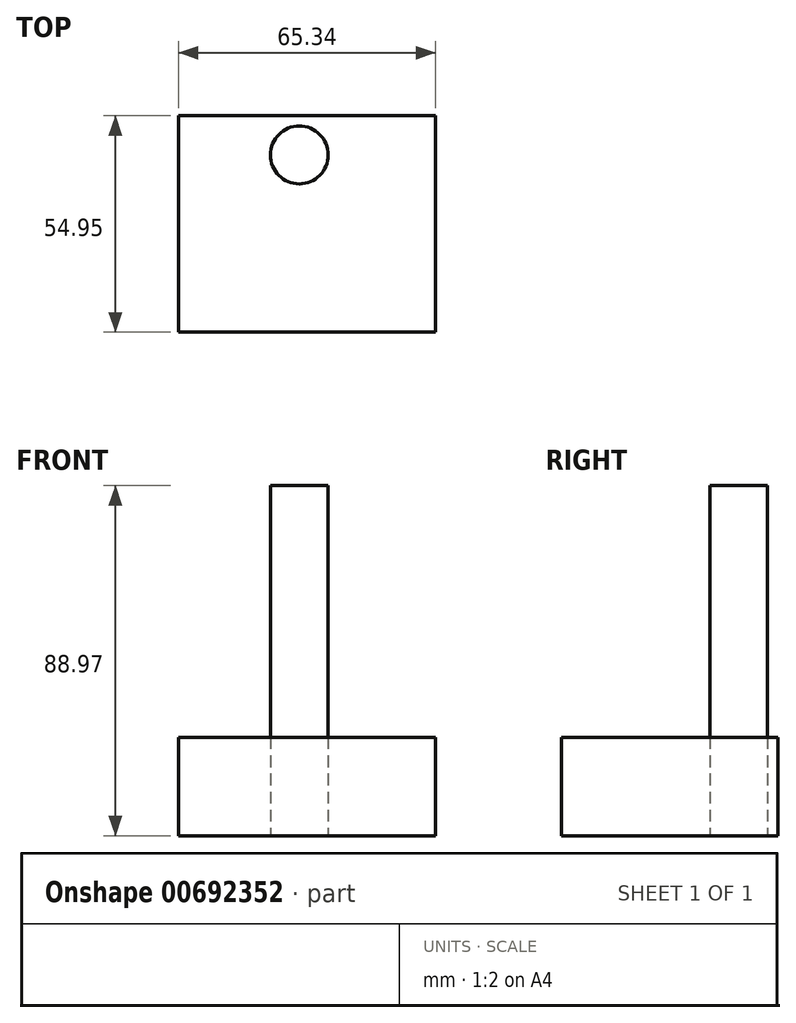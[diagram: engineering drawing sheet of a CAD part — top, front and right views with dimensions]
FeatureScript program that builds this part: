
annotation { "Feature Type Name" : "Feature", "Feature Type Description" : "" }
export const myFeature = defineFeature(function(context is Context, id is Id, definition is map)
    precondition{}
    {
        {
            var Q0;
            Q0=qCreatedBy(makeId("Top.planeOp"),FACE);
            var sketch = newSketch(context, id + "F0", { "sketchPlane" : qUnion([Q0])});
            skLineSegment(sketch, "E0.bottom", {"start": v(-26.18, 32.67) * mm, "end": v(39.16, 32.67) * mm});
            skLineSegment(sketch, "E0.top", {"start": v(-26.18, -22.28) * mm, "end": v(39.16, -22.28) * mm});
            skLineSegment(sketch, "E0.left", {"start": v(-26.18, 32.67) * mm, "end": v(-26.18, -22.28) * mm});
            skLineSegment(sketch, "E0.right", {"start": v(39.16, 32.67) * mm, "end": v(39.16, -22.28) * mm});
            skSolve(sketch);
        }
        {
            var Q0;
            Q0=makeQuery(id+"F0.imprint","IMPRINT",FACE,{"disambiguationData":[TD([[makeQuery(id+"F0.imprint","IMPRINT",EDGE,{"derivedFrom":sQuery(id+"F0.wireOp",EDGE,"E0.bottom")}),-1.0]])]});
            extrude(context, id + "F1", {"entities" : qUnion([Q0]), "depth" : 25 * mm, "offsetDistance" : 25 * mm});
        }
        {
            var Q0;
            Q0=qCreatedBy(makeId("Top.planeOp"),FACE);
            var sketch = newSketch(context, id + "F2", { "sketchPlane" : qUnion([Q0])});
            skCircle(sketch, "E1", {"center": v(4.54, 22.72) * mm, "radius": 7.34 * mm});
            skSolve(sketch);
        }
        {
            var Q0;
            Q0 = qSketchRegion(id + "F2", true);
            extrude(context, id + "F3", {"entities" : qUnion([Q0]), "endBound" : BoundingType.THROUGH_ALL, "depth" : 25 * mm, "offsetDistance" : 25 * mm});
        }
    });
